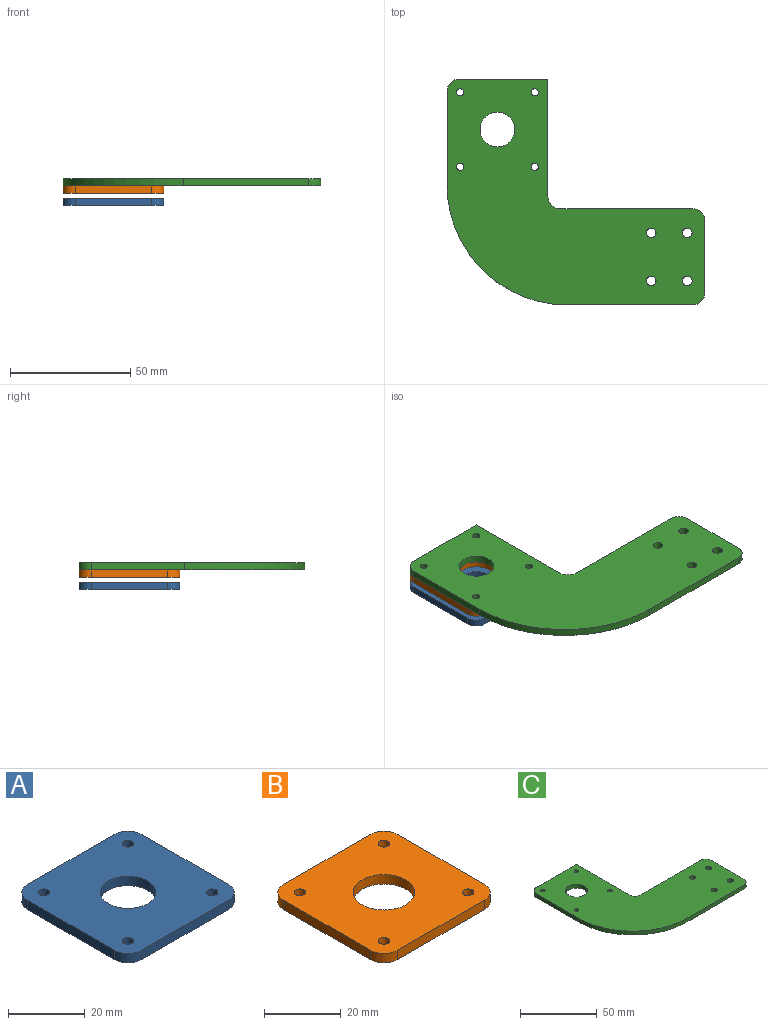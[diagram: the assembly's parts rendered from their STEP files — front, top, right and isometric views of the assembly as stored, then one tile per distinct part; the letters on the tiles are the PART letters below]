
ASSEMBLY  parts=3 mates=2
PART A: 15 faces, bbox 42x42x3 mm
  f0: plane 32x3mm, normal (0,-1,0), area 96mm2, adj f4,f5,f11,f14
  f1: plane 32x3mm, normal (1,0,0), area 96mm2, adj f4,f5,f11,f12
  f2: plane 32x3mm, normal (0,1,0), area 96mm2, adj f4,f5,f12,f13
  f3: plane 32x3mm, normal (-1,0,0), area 96mm2, adj f4,f5,f13,f14
  f4: plane 42x42mm, normal (0,0,1), area 1549.1mm2, adj f0,f1,f2,f3,f6,f7,f8,f9
  f5: plane 42x42mm, normal (0,0,-1), area 1549.1mm2, adj f0,f1,f2,f3,f6,f7,f8,f9
  f6: cylinder r=7.25mm len=14.5mm, axis (0,0,1), area 136.7mm2, adj f4,f5
  f7: cylinder r=1.5mm len=3mm, axis (0,0,-1), area 28.3mm2, adj f4,f5
  f8: cylinder r=1.5mm len=3mm, axis (0,0,-1), area 28.3mm2, adj f4,f5
  f9: cylinder r=1.5mm len=3mm, axis (0,0,-1), area 28.3mm2, adj f4,f5
  f10: cylinder r=1.5mm len=3mm, axis (0,0,-1), area 28.3mm2, adj f4,f5
  f11: cylinder r=5mm len=5mm, axis (0,0,-1), area 23.6mm2, adj f0,f1,f4,f5
  f12: cylinder r=5mm len=5mm, axis (0,0,1), area 23.6mm2, adj f1,f2,f4,f5
  f13: cylinder r=5mm len=5mm, axis (0,0,-1), area 23.6mm2, adj f2,f3,f4,f5
  f14: cylinder r=5mm len=5mm, axis (0,0,1), area 23.6mm2, adj f0,f3,f4,f5
PART B: 15 faces, bbox 42x42x3 mm
  f0: plane 32x3mm, normal (0,-1,0), area 96mm2, adj f4,f5,f12,f14
  f1: plane 32x3mm, normal (1,0,0), area 96mm2, adj f4,f5,f13,f14
  f2: plane 32x3mm, normal (0,1,0), area 96mm2, adj f4,f5,f11,f13
  f3: plane 32x3mm, normal (-1,0,0), area 96mm2, adj f4,f5,f11,f12
  f4: plane 42x42mm, normal (0,0,1), area 1513.2mm2, adj f0,f1,f2,f3,f6,f7,f8,f9
  f5: plane 42x42mm, normal (0,0,-1), area 1513.2mm2, adj f0,f1,f2,f3,f6,f7,f8,f9
  f6: cylinder r=8mm len=16mm, axis (0,0,1), area 150.8mm2, adj f4,f5
  f7: cylinder r=1.5mm len=3mm, axis (0,0,-1), area 28.3mm2, adj f4,f5
  f8: cylinder r=1.5mm len=3mm, axis (0,0,-1), area 28.3mm2, adj f4,f5
  f9: cylinder r=1.5mm len=3mm, axis (0,0,-1), area 28.3mm2, adj f4,f5
  f10: cylinder r=1.5mm len=3mm, axis (0,0,-1), area 28.3mm2, adj f4,f5
  f11: cylinder r=5mm len=5mm, axis (0,0,-1), area 23.6mm2, adj f2,f3,f4,f5
  f12: cylinder r=5mm len=5mm, axis (0,0,1), area 23.6mm2, adj f0,f3,f4,f5
  f13: cylinder r=5mm len=5mm, axis (0,0,1), area 23.6mm2, adj f1,f2,f4,f5
  f14: cylinder r=5mm len=5mm, axis (0,0,-1), area 23.6mm2, adj f0,f1,f4,f5
PART C: 22 faces, bbox 107.4x94x3 mm
  f0: plane 55.37x3mm, normal (0,1,0), area 166.1mm2, adj f6,f7,f20,f21
  f1: plane 49x3mm, normal (1,0,0), area 147mm2, adj f2,f6,f7,f21
  f2: plane 37x3mm, normal (0,1,0), area 111mm2, adj f1,f6,f7,f18
  f3: plane 39x3mm, normal (-1,0,0), area 117mm2, adj f6,f7,f8,f18
  f4: plane 52.37x3mm, normal (0,-1,0), area 157.1mm2, adj f6,f7,f8,f19
  f5: plane 30x3mm, normal (1,0,0), area 90mm2, adj f6,f7,f19,f20
  f6: plane 107.37x94mm, normal (0,0,1), area 5771.7mm2, adj f0,f1,f2,f3,f4,f5,f8,f9
  f7: plane 107.37x94mm, normal (0,0,-1), area 5771.7mm2, adj f0,f1,f2,f3,f4,f5,f8,f9
  f8: cylinder r=50mm len=50mm, axis (0,0,-1), area 235.6mm2, adj f3,f4,f6,f7
  f9: cylinder r=7.25mm len=14.5mm, axis (0,0,1), area 136.7mm2, adj f6,f7
  f10: cylinder r=2mm len=4mm, axis (0,0,-1), area 37.7mm2, adj f6,f7
  f11: cylinder r=2mm len=4mm, axis (0,0,-1), area 37.7mm2, adj f6,f7
  f12: cylinder r=2mm len=4mm, axis (0,0,-1), area 37.7mm2, adj f6,f7
  f13: cylinder r=2mm len=4mm, axis (0,0,-1), area 37.7mm2, adj f6,f7
  f14: cylinder r=1.5mm len=3mm, axis (0,0,-1), area 28.3mm2, adj f6,f7
  f15: cylinder r=1.5mm len=3mm, axis (0,0,-1), area 28.3mm2, adj f6,f7
  f16: cylinder r=1.5mm len=3mm, axis (0,0,-1), area 28.3mm2, adj f6,f7
  f17: cylinder r=1.5mm len=3mm, axis (0,0,-1), area 28.3mm2, adj f6,f7
  f18: cylinder r=5mm len=5mm, axis (0,0,-1), area 23.6mm2, adj f2,f3,f6,f7
  f19: cylinder r=5mm len=5mm, axis (0,0,1), area 23.6mm2, adj f4,f5,f6,f7
  f20: cylinder r=5mm len=5mm, axis (0,0,-1), area 23.6mm2, adj f0,f5,f6,f7
  f21: cylinder r=5mm len=5mm, axis (0,0,1), area 23.6mm2, adj f0,f1,f6,f7
PLACE A t=(-14.06,-11.93,-63.08)mm
PLACE B t=(-14.06,-11.93,-53.88)mm
PLACE C t=(-14.06,-11.93,-60.88)mm
MATE fastened B.f6 <-> C.f9  axis (0,0,1) through (-14.06,-11.93,-35.88)mm
MATE fastened C.f9 <-> A.f6  axis (0,0,-1) through (-14.06,-11.93,-35.88)mm
